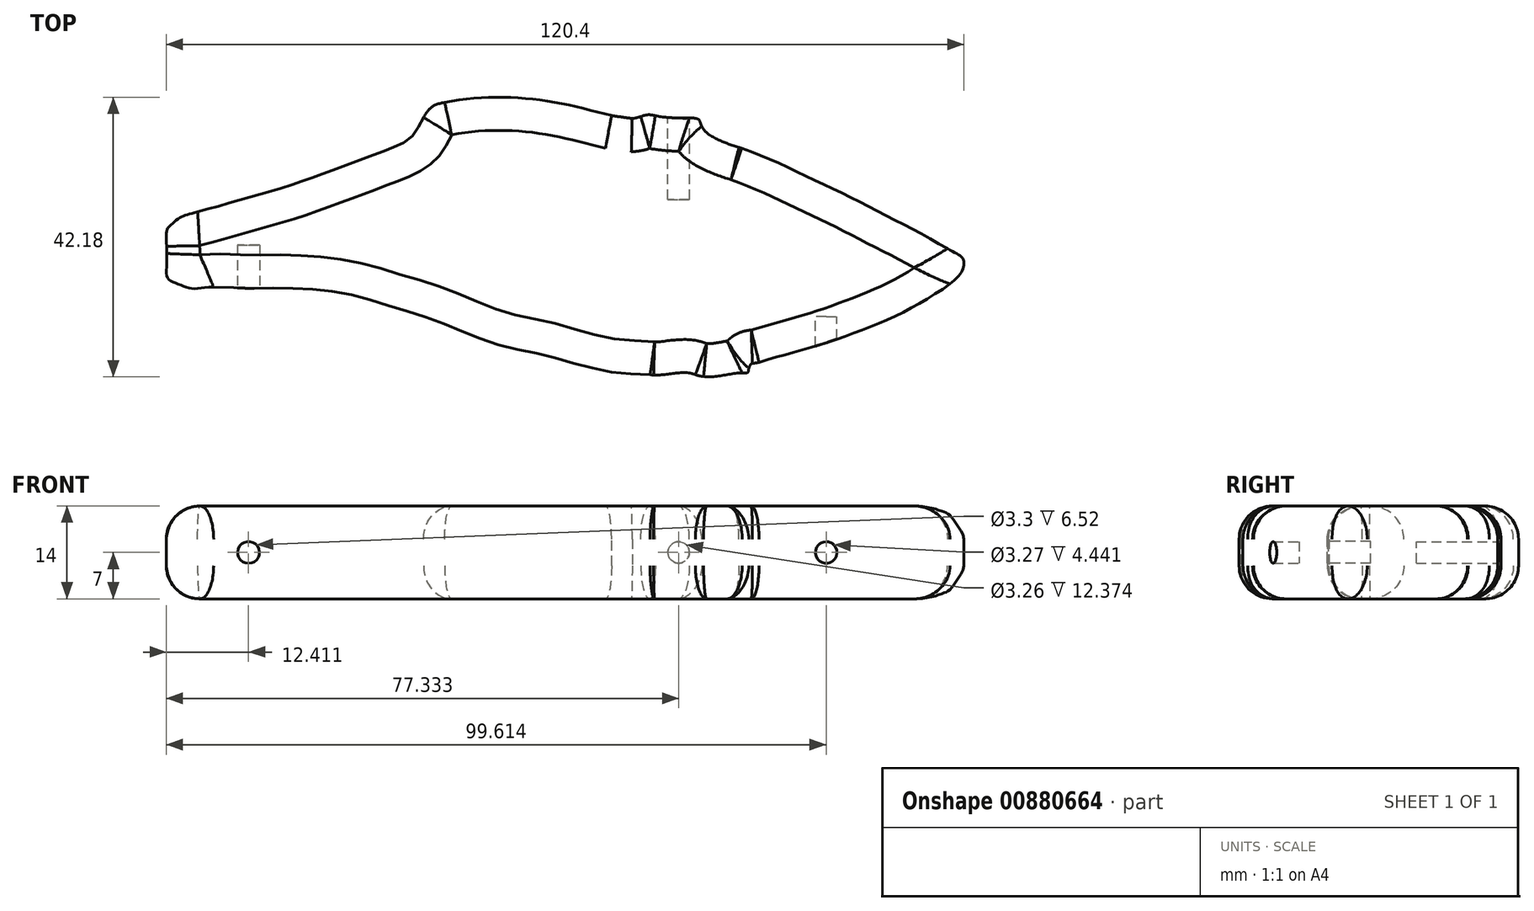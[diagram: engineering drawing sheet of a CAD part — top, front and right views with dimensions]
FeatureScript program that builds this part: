
annotation { "Feature Type Name" : "Feature", "Feature Type Description" : "" }
export const myFeature = defineFeature(function(context is Context, id is Id, definition is map)
    precondition{}
    {
        {
            var Q0;
            Q0=qCreatedBy(makeId("Top.planeOp"),FACE);
            var sketch = newSketch(context, id + "F0", { "sketchPlane" : qUnion([Q0])});
            skPoint(sketch, "E0.2.internal.orphan", {"position": v(-52.4, 63.58) * mm});
            skPoint(sketch, "E0.5.internal.orphan", {"position": v(27.56, 37.73) * mm});
            skPoint(sketch, "E1.end.orphan", {"position": v(27.56, 33.82) * mm});
            skPoint(sketch, "E1.start.orphan", {"position": v(-144.08, 63.58) * mm});
            skFitSpline(sketch, "E2", {"points": [v(-61.68, 4.45) * mm, v(-64.33, 4.24) * mm, v(-65.98, 4.77) * mm, v(-67.52, 5.4) * mm, v(-68.11, 6.17) * mm, v(-68.11, 8.69) * mm, v(-68.14, 12.97) * mm, v(-67.72, 13.64) * mm, v(-66.19, 14.92) * mm, v(-64.5, 15.54) * mm, v(-59.33, 16.96) * mm, v(-51.59, 19.19) * mm, v(-46.31, 20.93) * mm, v(-38.82, 23.7) * mm, v(-33.6, 25.72) * mm, v(-31.1, 27.2) * mm, v(-29.51, 29.82) * mm, v(-28.11, 31.66) * mm, v(-25.96, 32.39) * mm, v(-20.55, 33.05) * mm, v(-14.25, 32.96) * mm, v(-10.42, 32.5) * mm, v(-6.5, 31.73) * mm, v(-0.97, 30.35) * mm, v(2.37, 29.94) * mm, v(4.37, 30.46) * mm, v(5.86, 30.28) * mm, v(10.03, 29.96) * mm, v(12.14, 29.8) * mm, v(12.48, 29.11) * mm, v(13.81, 27.44) * mm, v(18.19, 25.56) * mm, v(18.53, 25.47) * mm, v(24.13, 23.22) * mm, v(27.63, 21.57) * mm, v(34.19, 18.48) * mm, v(38.66, 16.18) * mm, v(43.31, 13.82) * mm, v(48.13, 11.2) * mm, v(50.83, 9.67) * mm, v(51.89, 9) * mm, v(52.2, 8.11) * mm, v(51.98, 7) * mm, v(51.18, 5.91) * mm, v(49.46, 4.5) * mm, v(46.09, 2.36) * mm, v(42.33, 0.32) * mm, v(35.89, -2.34) * mm, v(29.3, -4.58) * mm, v(23.16, -6.3) * mm, v(20.67, -7) * mm, v(20.14, -7.08) * mm, v(19.7, -7.93) * mm, v(19.59, -8.39) * mm, v(18.4, -8.48) * mm, v(15.74, -8.87) * mm, v(14.04, -9.05) * mm, v(12.23, -8.92) * mm, v(10.9, -8.5) * mm, v(8.86, -8.5) * mm, v(6.98, -8.73) * mm, v(6.34, -8.78) * mm, v(5.12, -8.78) * mm, v(4.76, -8.73) * mm, v(1.23, -8.57) * mm, v(-1.23, -8.3) * mm, v(-7.23, -6.9) * mm, v(-11.5, -5.66) * mm, v(-17.4, -4.4) * mm, v(-25.57, -1.35) * mm, v(-29.08, 0) * mm, v(-35.17, 1.86) * mm, v(-40.33, 3.32) * mm, v(-45.65, 4.08) * mm, v(-51.4, 4.36) * mm, v(-55.67, 4.29) * mm, v(-61.68, 4.45) * mm]});
            skFitSpline(sketch, "E3", {"points": [v(20.14, -7.08) * mm, v(18.27, -7.45) * mm, v(15.61, -7.78) * mm, v(12.82, -8.27) * mm, v(10.9, -8.5) * mm], "startDerivative": vector(-7.89, -1.76) * mm, "endDerivative": vector(-8.02, -0.8) * mm});
            skFitSpline(sketch, "E4", {"points": [v(13.81, 27.44) * mm, v(7.62, 29.08) * mm, v(4.12, 29.64) * mm, v(-0.97, 30.35) * mm], "startDerivative": vector(-17.71, 5.05) * mm, "endDerivative": vector(-15.99, 2.27) * mm});
            skSolve(sketch);
        }
        {
            var Q0;
            Q0 = qSketchRegion(id + "F0", true);
            extrude(context, id + "F1", {"entities" : qUnion([Q0]), "depth" : 7 * mm, "offsetDistance" : 25.4 * mm});
        }
        {
            var Q0;
            Q0=makeQuery(id+"F1.opExtrude","CAP_EDGE",EDGE,{"disambiguationData":[OSD([sQuery(id+"F0.wireOp",EDGE,"E2")])],"isStart":false});
            var Q1;
            Q1=makeQuery(id+"F1.opExtrude","CAP_EDGE",EDGE,{"disambiguationData":[OSD([sQuery(id+"F0.wireOp",EDGE,"E4")])],"isStart":false});
            var Q2;
            Q2=makeQuery(id+"F1.opExtrude","CAP_EDGE",EDGE,{"disambiguationData":[OSD([sQuery(id+"F0.wireOp",EDGE,"E2")])],"isStart":false});
            var Q3;
            Q3=makeQuery(id+"F1.opExtrude","CAP_EDGE",EDGE,{"disambiguationData":[OSD([sQuery(id+"F0.wireOp",EDGE,"E3")])],"isStart":false});
            fillet(context, id + "F2", {"entities" : qUnion([Q0, Q1, Q2, Q3]), "radius" : 5 * mm, "tangentPropagation" : true, "allowEdgeOverflow" : false});
        }
        {
            var Q0;
            Q0=makeQuery(id+"F1.opExtrude","SWEPT_BODY",BODY,{"disambiguationData":[OSD([sQuery(id+"F0.wireOp",EDGE,"E2"),sQuery(id+"F0.wireOp",EDGE,"E3"),sQuery(id+"F0.wireOp",EDGE,"E4"),sQuery(id+"F0.wireOp",EDGE,"E2")])]});
            var Q1;
            Q1=makeQuery(id+"F1.opExtrude","CAP_FACE",FACE,{"disambiguationData":[OSD([sQuery(id+"F0.wireOp",EDGE,"E2"),sQuery(id+"F0.wireOp",EDGE,"E3"),sQuery(id+"F0.wireOp",EDGE,"E4"),sQuery(id+"F0.wireOp",EDGE,"E2")])],"isStart":true});
            mirror(context, id + "F3", {"operationType" : NewBodyOperationType.ADD, "entities" : qUnion([Q0]), "mirrorPlane" : qUnion([Q1])});
        }
        {
            var Q0;
            Q0=qCreatedBy(makeId("Front.planeOp"),FACE);
            var sketch = newSketch(context, id + "F4", { "sketchPlane" : qUnion([Q0])});
            skCircle(sketch, "E5", {"center": v(-55.78, 0) * mm, "radius": 1.65 * mm});
            skSolve(sketch);
        }
        {
            var Q0;
            Q0=makeQuery(id+"F4.imprint","IMPRINT",FACE,{"disambiguationData":[TD([[makeQuery(id+"F4.imprint","IMPRINT",EDGE,{"derivedFrom":sQuery(id+"F4.wireOp",EDGE,"E5")}),1.0]])]});
            extrude(context, id + "F5", {"entities" : qUnion([Q0]), "operationType" : NewBodyOperationType.REMOVE, "oppositeDirection" : true, "depth" : 10.8 * mm, "offsetDistance" : 25 * mm});
        }
        {
            var Q0;
            Q0=qCreatedBy(makeId("Front.planeOp"),FACE);
            var sketch = newSketch(context, id + "F6", { "sketchPlane" : qUnion([Q0])});
            skCircle(sketch, "E6", {"center": v(31.42, 0) * mm, "radius": 1.63 * mm});
            skSolve(sketch);
        }
        {
            var Q0;
            Q0 = qSketchRegion(id + "F6", true);
            extrude(context, id + "F7", {"entities" : qUnion([Q0]), "operationType" : NewBodyOperationType.REMOVE, "depth" : 10.7 * mm, "offsetDistance" : 25 * mm});
        }
        {
            var Q0;
            Q0=qCreatedBy(makeId("Front.planeOp"),FACE);
            var sketch = newSketch(context, id + "F8", { "sketchPlane" : qUnion([Q0])});
            skCircle(sketch, "E7", {"center": v(9.14, 0) * mm, "radius": 1.63 * mm});
            skSolve(sketch);
        }
        {
            var Q0;
            Q0 = qSketchRegion(id + "F8", true);
            extrude(context, id + "F9", {"entities" : qUnion([Q0]), "operationType" : NewBodyOperationType.ADD, "oppositeDirection" : true, "depth" : 36.5 * mm, "offsetDistance" : 25 * mm});
        }
        {
            var Q0;
            Q0=makeQuery(id+"F9.opExtrude","CAP_FACE",FACE,{"disambiguationData":[OSD([sQuery(id+"F8.wireOp",EDGE,"E7")])],"isStart":false});
            extrude(context, id + "F10", {"entities" : qUnion([Q0]), "operationType" : NewBodyOperationType.REMOVE, "oppositeDirection" : true, "depth" : 18.8 * mm, "offsetDistance" : 25 * mm});
        }
    });
